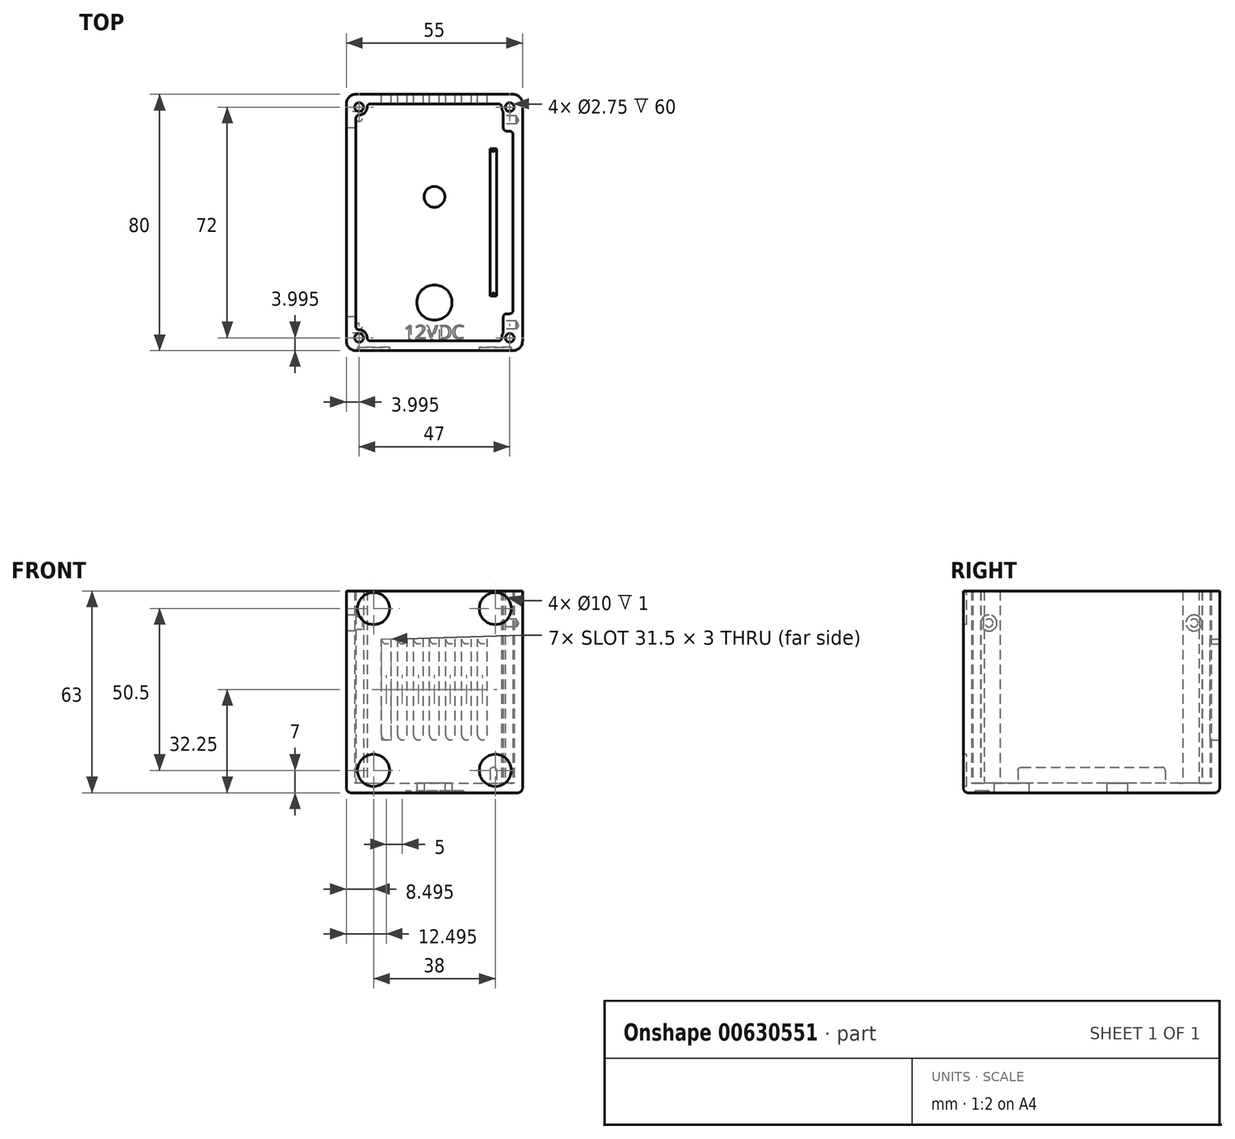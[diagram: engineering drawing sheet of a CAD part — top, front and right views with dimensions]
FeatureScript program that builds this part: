
annotation { "Feature Type Name" : "Feature", "Feature Type Description" : "" }
export const myFeature = defineFeature(function(context is Context, id is Id, definition is map)
    precondition{}
    {
        {
            var Q0;
            Q0=qCreatedBy(makeId("Top.planeOp"),FACE);
            var sketch = newSketch(context, id + "F0", { "sketchPlane" : qUnion([Q0])});
            skLineSegment(sketch, "E0.bottom", {"start": v(-24.01, 49.08) * mm, "end": v(30.99, 49.08) * mm});
            skLineSegment(sketch, "E0.top", {"start": v(-24.01, -30.92) * mm, "end": v(30.99, -30.92) * mm});
            skLineSegment(sketch, "E0.left", {"start": v(-24.01, 49.08) * mm, "end": v(-24.01, -30.92) * mm});
            skLineSegment(sketch, "E0.right", {"start": v(30.99, 49.08) * mm, "end": v(30.99, -30.92) * mm});
            skCircle(sketch, "E1", {"center": v(3.49, -15.92) * mm, "radius": 5.5 * mm});
            skCircle(sketch, "E2", {"center": v(3.49, 17.08) * mm, "radius": 3.25 * mm});
            skSolve(sketch);
        }
        {
            var Q0;
            Q0=makeQuery(id+"F0.imprint","IMPRINT",FACE,{"disambiguationData":[TD([[makeQuery(id+"F0.imprint","IMPRINT",EDGE,{"derivedFrom":sQuery(id+"F0.wireOp",EDGE,"E0.bottom")}),-1.0]])]});
            extrude(context, id + "F1", {"entities" : qUnion([Q0]), "depth" : 3 * mm, "offsetDistance" : 25 * mm});
        }
        {
            var Q0;
            Q0=makeQuery(id+"F1.opExtrude","CAP_FACE",FACE,{"disambiguationData":[OSD([sQuery(id+"F0.wireOp",EDGE,"E0.bottom"),sQuery(id+"F0.wireOp",EDGE,"E0.top"),sQuery(id+"F0.wireOp",EDGE,"E0.left"),sQuery(id+"F0.wireOp",EDGE,"E0.right"),sQuery(id+"F0.wireOp",EDGE,"E1")])],"isStart":false});
            var sketch = newSketch(context, id + "F2", { "sketchPlane" : qUnion([Q0])});
            skLineSegment(sketch, "E3.bottom", {"start": v(-24.01, 49.08) * mm, "end": v(30.99, 49.08) * mm});
            skLineSegment(sketch, "E3.top", {"start": v(-24.01, -30.92) * mm, "end": v(30.99, -30.92) * mm});
            skLineSegment(sketch, "E3.left", {"start": v(-24.01, 49.08) * mm, "end": v(-24.01, -30.92) * mm});
            skLineSegment(sketch, "E3.right", {"start": v(30.99, 49.08) * mm, "end": v(30.99, -30.92) * mm});
            skLineSegment(sketch, "E4.bottom", {"start": v(-16.51, 46.08) * mm, "end": v(23.49, 46.08) * mm});
            skLineSegment(sketch, "E4.top", {"start": v(-16.51, -27.92) * mm, "end": v(23.49, -27.92) * mm});
            skLineSegment(sketch, "E4.left", {"start": v(-21.01, 41.58) * mm, "end": v(-21.01, -23.42) * mm});
            skLineSegment(sketch, "E4.right", {"start": v(27.99, 36.58) * mm, "end": v(27.99, -18.42) * mm});
            skCircle(sketch, "E5", {"center": v(-20.01, 45.08) * mm, "radius": 1.38 * mm});
            skCircle(sketch, "E6", {"center": v(-20.01, 45.08) * mm, "radius": 2.5 * mm});
            skCircle(sketch, "E7", {"center": v(26.99, 45.08) * mm, "radius": 1.38 * mm});
            skCircle(sketch, "E8", {"center": v(26.99, 45.08) * mm, "radius": 2.5 * mm});
            skCircle(sketch, "E9", {"center": v(-20.01, -26.92) * mm, "radius": 1.38 * mm});
            skCircle(sketch, "E10", {"center": v(-20.01, -26.92) * mm, "radius": 2.5 * mm});
            skCircle(sketch, "E11", {"center": v(26.99, -26.92) * mm, "radius": 1.38 * mm});
            skCircle(sketch, "E12", {"center": v(26.99, -26.92) * mm, "radius": 2.5 * mm});
            skLineSegment(sketch, "E13", {"start": v(-20.01, 42.58) * mm, "end": v(-20.01, 42.58) * mm});
            skLineSegment(sketch, "E14", {"start": v(-17.51, 45.08) * mm, "end": v(-17.51, 45.08) * mm});
            skArc(sketch, "E15.filletArc", {"start": v(-16.51, 46.08) * mm, "mid": v(-17.22, 45.78) * mm, "end": v(-17.51, 45.08) * mm});
            skArc(sketch, "E16.filletArc", {"start": v(-20.01, 42.58) * mm, "mid": v(-20.72, 42.28) * mm, "end": v(-21.01, 41.58) * mm});
            skLineSegment(sketch, "E17", {"start": v(24.49, 45.08) * mm, "end": v(24.49, 45.08) * mm});
            skLineSegment(sketch, "E18", {"start": v(26.99, 42.58) * mm, "end": v(26.99, 42.58) * mm});
            skArc(sketch, "E19.filletArc", {"start": v(24.49, 45.08) * mm, "mid": v(24.2, 45.78) * mm, "end": v(23.49, 46.08) * mm});
            skArc(sketch, "E20.filletArc", {"start": v(27.99, 41.58) * mm, "mid": v(27.7, 42.28) * mm, "end": v(26.99, 42.58) * mm});
            skLineSegment(sketch, "E21", {"start": v(-20.01, -24.42) * mm, "end": v(-20.01, -24.42) * mm});
            skLineSegment(sketch, "E22", {"start": v(-17.51, -26.92) * mm, "end": v(-17.51, -26.92) * mm});
            skArc(sketch, "E23.filletArc", {"start": v(-21.01, -23.42) * mm, "mid": v(-20.72, -24.13) * mm, "end": v(-20.01, -24.42) * mm});
            skArc(sketch, "E24.filletArc", {"start": v(-17.51, -26.92) * mm, "mid": v(-17.22, -27.63) * mm, "end": v(-16.51, -27.92) * mm});
            skLineSegment(sketch, "E25", {"start": v(24.49, -26.92) * mm, "end": v(24.49, -26.92) * mm});
            skLineSegment(sketch, "E26", {"start": v(26.99, -24.42) * mm, "end": v(26.99, -24.42) * mm});
            skArc(sketch, "E27.filletArc", {"start": v(23.49, -27.92) * mm, "mid": v(24.2, -27.63) * mm, "end": v(24.49, -26.92) * mm});
            skLineSegment(sketch, "E28.bottom", {"start": v(27.99, 43.58) * mm, "end": v(24.99, 43.58) * mm});
            skLineSegment(sketch, "E28.top", {"start": v(26.99, 37.58) * mm, "end": v(25.99, 37.58) * mm});
            skLineSegment(sketch, "E28.left", {"start": v(27.99, 43.58) * mm, "end": v(27.99, 37.58) * mm});
            skLineSegment(sketch, "E28.right", {"start": v(24.99, 43.58) * mm, "end": v(24.99, 38.58) * mm});
            skLineSegment(sketch, "E29.bottom", {"start": v(26.99, -19.42) * mm, "end": v(25.99, -19.42) * mm});
            skLineSegment(sketch, "E29.top", {"start": v(27.99, -25.42) * mm, "end": v(24.99, -25.42) * mm});
            skLineSegment(sketch, "E29.left", {"start": v(27.99, -19.42) * mm, "end": v(27.99, -25.42) * mm});
            skLineSegment(sketch, "E29.right", {"start": v(24.99, -20.42) * mm, "end": v(24.99, -25.42) * mm});
            skArc(sketch, "E30.filletArc", {"start": v(26.99, -19.42) * mm, "mid": v(27.7, -19.13) * mm, "end": v(27.99, -18.42) * mm});
            skPoint(sketch, "E31.visualSharp", {"position": v(24.99, -19.42) * mm});
            skArc(sketch, "E31.filletArc", {"start": v(25.99, -19.42) * mm, "mid": v(25.28, -19.72) * mm, "end": v(24.99, -20.42) * mm});
            skPoint(sketch, "E32.newPointA", {"position": v(27.99, 37.58) * mm});
            skArc(sketch, "E32.filletArc", {"start": v(27.99, 36.58) * mm, "mid": v(27.7, 37.28) * mm, "end": v(26.99, 37.58) * mm});
            skPoint(sketch, "E33.visualSharp", {"position": v(24.99, 37.58) * mm});
            skArc(sketch, "E33.filletArc", {"start": v(24.99, 38.58) * mm, "mid": v(25.28, 37.87) * mm, "end": v(25.99, 37.58) * mm});
            skLineSegment(sketch, "E34.bottom", {"start": v(20.89, 32.08) * mm, "end": v(22.89, 32.08) * mm});
            skLineSegment(sketch, "E34.top", {"start": v(20.89, -13.84) * mm, "end": v(22.89, -13.84) * mm});
            skLineSegment(sketch, "E34.left", {"start": v(20.89, 32.08) * mm, "end": v(20.89, -13.84) * mm});
            skLineSegment(sketch, "E34.right", {"start": v(22.89, 32.08) * mm, "end": v(22.89, -13.84) * mm});
            skSolve(sketch);
        }
        {
            var Q0;
            Q0=makeQuery(id+"F1.opExtrude","SWEPT_EDGE",EDGE,{"disambiguationData":[OSD([sQuery(id+"F0.wireOp",EDGE,"E0.top"),sQuery(id+"F0.wireOp",EDGE,"E0.right")])]});
            var Q1;
            Q1=makeQuery(id+"F1.opExtrude","SWEPT_EDGE",EDGE,{"disambiguationData":[OSD([sQuery(id+"F0.wireOp",EDGE,"E0.top"),sQuery(id+"F0.wireOp",EDGE,"E0.left")])]});
            var Q2;
            Q2=makeQuery(id+"F1.opExtrude","SWEPT_EDGE",EDGE,{"disambiguationData":[OSD([sQuery(id+"F0.wireOp",EDGE,"E0.bottom"),sQuery(id+"F0.wireOp",EDGE,"E0.left")])]});
            var Q3;
            Q3=makeQuery(id+"F1.opExtrude","SWEPT_EDGE",EDGE,{"disambiguationData":[OSD([sQuery(id+"F0.wireOp",EDGE,"E0.bottom"),sQuery(id+"F0.wireOp",EDGE,"E0.right")])]});
            fillet(context, id + "F3", {"entities" : qUnion([Q0, Q1, Q2, Q3]), "radius" : 3 * mm, "tangentPropagation" : true, "allowEdgeOverflow" : false});
        }
        {
            var Q0;
            Q0=makeQuery(id+"F1.opExtrude","CAP_EDGE",EDGE,{"disambiguationData":[OSD([sQuery(id+"F0.wireOp",EDGE,"E0.right")])],"isStart":true});
            fillet(context, id + "F4", {"entities" : qUnion([Q0]), "radius" : 1.5 * mm, "tangentPropagation" : true, "allowEdgeOverflow" : false});
        }
        {
            var Q0;
            Q0=makeQuery(id+"F2.imprint","IMPRINT",FACE,{"disambiguationData":[TD([[makeQuery(id+"F2.imprint","IMPRINT",EDGE,{"derivedFrom":sQuery(id+"F2.wireOp",EDGE,"E9")}),-1.0]])]});
            var Q1;
            Q1=makeQuery(id+"F2.imprint","IMPRINT",FACE,{"disambiguationData":[TD([[makeQuery(id+"F2.imprint","IMPRINT",EDGE,{"derivedFrom":sQuery(id+"F2.wireOp",EDGE,"E11")}),-1.0]])]});
            var Q2;
            {var subQ0=sQuery(id+"F2.wireOp",EDGE,"E29.top");Q2=makeQuery(id+"F2.imprint","IMPRINT",FACE,{"disambiguationData":[TD([[makeQuery(id+"F2.imprint","IMPRINT",EDGE,{"derivedFrom":subQ0}),-1.0]])]});}
            var Q3;
            Q3=makeQuery(id+"F2.imprint","IMPRINT",FACE,{"disambiguationData":[TD([[makeQuery(id+"F2.imprint","IMPRINT",EDGE,{"derivedFrom":sQuery(id+"F2.wireOp",EDGE,"E5")}),-1.0]])]});
            var Q4;
            Q4=makeQuery(id+"F2.imprint","IMPRINT",FACE,{"disambiguationData":[TD([[makeQuery(id+"F2.imprint","IMPRINT",EDGE,{"derivedFrom":sQuery(id+"F2.wireOp",EDGE,"E7")}),-1.0]])]});
            var Q5;
            {var subQ2=sQuery(id+"F2.wireOp",EDGE,"E28.bottom");Q5=makeQuery(id+"F2.imprint","IMPRINT",FACE,{"disambiguationData":[TD([[makeQuery(id+"F2.imprint","IMPRINT",EDGE,{"derivedFrom":subQ2}),1.0]])]});}
            var Q6;
            Q6=makeQuery(id+"F2.imprint","IMPRINT",FACE,{"disambiguationData":[TD([[makeQuery(id+"F2.imprint","IMPRINT",EDGE,{"derivedFrom":sQuery(id+"F2.wireOp",EDGE,"E3.bottom")}),-1.0]])]});
            var Q7;
            {var subQ0=sQuery(id+"F2.wireOp",EDGE,"E20.filletArc");Q7=makeQuery(id+"F2.imprint","IMPRINT",FACE,{"disambiguationData":[TD([[makeQuery(id+"F2.imprint","IMPRINT",EDGE,{"derivedFrom":subQ0}),-1.0]])]});}
            extrude(context, id + "F5", {"entities" : qUnion([Q0, Q1, Q2, Q3, Q4, Q5, Q6, Q7]), "operationType" : NewBodyOperationType.ADD, "depth" : 60 * mm, "offsetDistance" : 25 * mm});
        }
        {
            var Q0;
            Q0=makeQuery(id+"F5.opExtrude","SWEPT_EDGE",EDGE,{"disambiguationData":[OSD([sQuery(id+"F2.wireOp",EDGE,"E3.bottom"),sQuery(id+"F2.wireOp",EDGE,"E3.left")])]});
            var Q1;
            Q1=makeQuery(id+"F5.opExtrude","SWEPT_EDGE",EDGE,{"disambiguationData":[OSD([sQuery(id+"F2.wireOp",EDGE,"E3.top"),sQuery(id+"F2.wireOp",EDGE,"E3.left")])]});
            var Q2;
            Q2=makeQuery(id+"F5.opExtrude","SWEPT_EDGE",EDGE,{"disambiguationData":[OSD([sQuery(id+"F2.wireOp",EDGE,"E3.bottom"),sQuery(id+"F2.wireOp",EDGE,"E3.right")])]});
            var Q3;
            Q3=makeQuery(id+"F5.opExtrude","SWEPT_EDGE",EDGE,{"disambiguationData":[OSD([sQuery(id+"F2.wireOp",EDGE,"E3.top"),sQuery(id+"F2.wireOp",EDGE,"E3.right")])]});
            fillet(context, id + "F6", {"entities" : qUnion([Q0, Q1, Q2, Q3]), "radius" : 3 * mm, "tangentPropagation" : true, "allowEdgeOverflow" : false});
        }
        {
            var Q0;
            Q0=makeQuery(id+"F5.opExtrude","SWEPT_FACE",FACE,{"disambiguationData":[OSD([sQuery(id+"F2.wireOp",EDGE,"E29.right")])]});
            var sketch = newSketch(context, id + "F7", { "sketchPlane" : qUnion([Q0])});
            skPoint(sketch, "E35", {"position": v(-41.08, 53) * mm});
            skPoint(sketch, "E36", {"position": v(-41.08, 8.5) * mm});
            skPoint(sketch, "E37", {"position": v(22.92, 8.5) * mm});
            skPoint(sketch, "E38", {"position": v(22.92, 53) * mm});
            skSolve(sketch);
        }
        {
            var Q0;
            Q0=sQuery(id+"F7.wireOp",VERTEX,"E35");
            var Q1;
            Q1=sQuery(id+"F7.wireOp",VERTEX,"E38");
            var Q2;
            Q2=makeQuery(id+"F1.opExtrude","SWEPT_BODY",BODY,{"disambiguationData":[OSD([sQuery(id+"F0.wireOp",EDGE,"E0.bottom"),sQuery(id+"F0.wireOp",EDGE,"E0.top"),sQuery(id+"F0.wireOp",EDGE,"E0.left"),sQuery(id+"F0.wireOp",EDGE,"E0.right"),sQuery(id+"F0.wireOp",EDGE,"E1")])]});
            hole(context, id + "F8", {"style" : HoleStyle.SIMPLE, "endStyle" : HoleEndStyle.BLIND, "holeDiameter" : 2.5 * mm, "majorDiameter" : 5 * mm, "holeDepth" : 4 * mm, "isTappedThrough" : true, "tappedDepth" : 12 * mm, "tapClearance" : 3, "locations" : qUnion([Q0, Q1]), "scope" : qUnion([Q2])});
        }
        {
            var Q0;
            Q0=makeQuery(id+"F5.boolean.opBoolean","MERGE",FACE,{"derivedFrom":[makeQuery(id+"F1.opExtrude","SWEPT_FACE",FACE,{"disambiguationData":[OSD([sQuery(id+"F0.wireOp",EDGE,"E0.bottom")])]}),makeQuery(id+"F5.opExtrude","SWEPT_FACE",FACE,{"disambiguationData":[OSD([sQuery(id+"F2.wireOp",EDGE,"E3.bottom")])]})]});
            var sketch = newSketch(context, id + "F9", { "sketchPlane" : qUnion([Q0])});
            skCircle(sketch, "E39", {"center": v(-18.49, 18) * mm, "radius": 1.5 * mm});
            skCircle(sketch, "E40.0.1.0", {"center": v(-18.49, 48) * mm, "radius": 1.5 * mm});
            skLineSegment(sketch, "E40.direction2", {"start": v(-18.49, 18) * mm, "end": v(-18.49, 48) * mm, "construction": true});
            skLineSegment(sketch, "E41", {"start": v(-16.99, 18) * mm, "end": v(-16.99, 48) * mm});
            skLineSegment(sketch, "E42", {"start": v(-19.99, 18) * mm, "end": v(-19.99, 48) * mm});
            skCircle(sketch, "E43.1.0.0", {"center": v(-13.49, 18) * mm, "radius": 1.5 * mm});
            skLineSegment(sketch, "E43.1.0.1", {"start": v(-11.99, 18) * mm, "end": v(-11.99, 48) * mm});
            skCircle(sketch, "E43.1.0.2", {"center": v(-13.49, 48) * mm, "radius": 1.5 * mm});
            skLineSegment(sketch, "E43.1.0.3", {"start": v(-14.99, 18) * mm, "end": v(-14.99, 48) * mm});
            skCircle(sketch, "E43.2.0.0", {"center": v(-8.49, 18) * mm, "radius": 1.5 * mm});
            skLineSegment(sketch, "E43.2.0.1", {"start": v(-6.99, 18) * mm, "end": v(-6.99, 48) * mm});
            skCircle(sketch, "E43.2.0.2", {"center": v(-8.49, 48) * mm, "radius": 1.5 * mm});
            skLineSegment(sketch, "E43.2.0.3", {"start": v(-9.99, 18) * mm, "end": v(-9.99, 48) * mm});
            skCircle(sketch, "E43.3.0.0", {"center": v(-3.49, 18) * mm, "radius": 1.5 * mm});
            skLineSegment(sketch, "E43.3.0.1", {"start": v(-1.99, 18) * mm, "end": v(-1.99, 48) * mm});
            skCircle(sketch, "E43.3.0.2", {"center": v(-3.49, 48) * mm, "radius": 1.5 * mm});
            skLineSegment(sketch, "E43.3.0.3", {"start": v(-4.99, 18) * mm, "end": v(-4.99, 48) * mm});
            skCircle(sketch, "E43.4.0.0", {"center": v(1.51, 18) * mm, "radius": 1.5 * mm});
            skLineSegment(sketch, "E43.4.0.1", {"start": v(3.01, 18) * mm, "end": v(3.01, 48) * mm});
            skCircle(sketch, "E43.4.0.2", {"center": v(1.51, 48) * mm, "radius": 1.5 * mm});
            skLineSegment(sketch, "E43.4.0.3", {"start": v(0.01, 18) * mm, "end": v(0.01, 48) * mm});
            skCircle(sketch, "E43.5.0.0", {"center": v(6.51, 18) * mm, "radius": 1.5 * mm});
            skLineSegment(sketch, "E43.5.0.1", {"start": v(8.01, 18) * mm, "end": v(8.01, 48) * mm});
            skCircle(sketch, "E43.5.0.2", {"center": v(6.51, 48) * mm, "radius": 1.5 * mm});
            skLineSegment(sketch, "E43.5.0.3", {"start": v(5.01, 18) * mm, "end": v(5.01, 48) * mm});
            skCircle(sketch, "E43.6.0.0", {"center": v(11.51, 18) * mm, "radius": 1.5 * mm});
            skLineSegment(sketch, "E43.6.0.1", {"start": v(13.01, 18) * mm, "end": v(13.01, 48) * mm});
            skCircle(sketch, "E43.6.0.2", {"center": v(11.51, 48) * mm, "radius": 1.5 * mm});
            skLineSegment(sketch, "E43.6.0.3", {"start": v(10.01, 18) * mm, "end": v(10.01, 48) * mm});
            skLineSegment(sketch, "E43.direction1", {"start": v(-18.49, 18) * mm, "end": v(-13.49, 18) * mm, "construction": true});
            skSolve(sketch);
        }
        {
            var Q0;
            {var subQ0=sQuery(id+"F9.wireOp",EDGE,"E43.6.0.1");Q0=makeQuery(id+"F9.imprint","IMPRINT",FACE,{"disambiguationData":[TD([[makeQuery(id+"F9.imprint","IMPRINT",EDGE,{"derivedFrom":subQ0}),1.0]])]});}
            var Q1;
            {var subQ0=sQuery(id+"F9.wireOp",EDGE,"E43.5.0.1");Q1=makeQuery(id+"F9.imprint","IMPRINT",FACE,{"disambiguationData":[TD([[makeQuery(id+"F9.imprint","IMPRINT",EDGE,{"derivedFrom":subQ0}),1.0]])]});}
            var Q2;
            {var subQ0=sQuery(id+"F9.wireOp",EDGE,"E43.4.0.1");Q2=makeQuery(id+"F9.imprint","IMPRINT",FACE,{"disambiguationData":[TD([[makeQuery(id+"F9.imprint","IMPRINT",EDGE,{"derivedFrom":subQ0}),1.0]])]});}
            var Q3;
            {var subQ0=sQuery(id+"F9.wireOp",EDGE,"E43.3.0.1");Q3=makeQuery(id+"F9.imprint","IMPRINT",FACE,{"disambiguationData":[TD([[makeQuery(id+"F9.imprint","IMPRINT",EDGE,{"derivedFrom":subQ0}),1.0]])]});}
            var Q4;
            {var subQ0=sQuery(id+"F9.wireOp",EDGE,"E43.2.0.1");Q4=makeQuery(id+"F9.imprint","IMPRINT",FACE,{"disambiguationData":[TD([[makeQuery(id+"F9.imprint","IMPRINT",EDGE,{"derivedFrom":subQ0}),1.0]])]});}
            var Q5;
            {var subQ0=sQuery(id+"F9.wireOp",EDGE,"E43.1.0.1");Q5=makeQuery(id+"F9.imprint","IMPRINT",FACE,{"disambiguationData":[TD([[makeQuery(id+"F9.imprint","IMPRINT",EDGE,{"derivedFrom":subQ0}),1.0]])]});}
            var Q6;
            {var subQ0=sQuery(id+"F9.wireOp",EDGE,"E41");Q6=makeQuery(id+"F9.imprint","IMPRINT",FACE,{"disambiguationData":[TD([[makeQuery(id+"F9.imprint","IMPRINT",EDGE,{"derivedFrom":subQ0}),1.0]])]});}
            var Q7;
            {var subQ0=sQuery(id+"F9.wireOp",EDGE,"E39");var subQ1=makeQuery(id+"F9.imprint","INTERSECT",VERTEX,{"derivedFrom":[subQ0,sQuery(id+"F9.wireOp",EDGE,"E41")]});Q7=makeQuery(id+"F9.imprint","IMPRINT",FACE,{"disambiguationData":[TD([[makeQuery(id+"F9.imprint","IMPRINT",EDGE,{"disambiguationData":[TD([[subQ1,-1.0]])],"derivedFrom":subQ0}),1.0]])]});}
            var Q8;
            {var subQ0=sQuery(id+"F9.wireOp",EDGE,"E43.1.0.0");var subQ1=makeQuery(id+"F9.imprint","INTERSECT",VERTEX,{"derivedFrom":[subQ0,sQuery(id+"F9.wireOp",EDGE,"E43.1.0.1")]});Q8=makeQuery(id+"F9.imprint","IMPRINT",FACE,{"disambiguationData":[TD([[makeQuery(id+"F9.imprint","IMPRINT",EDGE,{"disambiguationData":[TD([[subQ1,-1.0]])],"derivedFrom":subQ0}),1.0]])]});}
            var Q9;
            {var subQ0=sQuery(id+"F9.wireOp",EDGE,"E43.2.0.0");var subQ1=makeQuery(id+"F9.imprint","INTERSECT",VERTEX,{"derivedFrom":[subQ0,sQuery(id+"F9.wireOp",EDGE,"E43.2.0.1")]});Q9=makeQuery(id+"F9.imprint","IMPRINT",FACE,{"disambiguationData":[TD([[makeQuery(id+"F9.imprint","IMPRINT",EDGE,{"disambiguationData":[TD([[subQ1,-1.0]])],"derivedFrom":subQ0}),1.0]])]});}
            var Q10;
            {var subQ0=sQuery(id+"F9.wireOp",EDGE,"E43.3.0.0");var subQ1=makeQuery(id+"F9.imprint","INTERSECT",VERTEX,{"derivedFrom":[subQ0,sQuery(id+"F9.wireOp",EDGE,"E43.3.0.1")]});Q10=makeQuery(id+"F9.imprint","IMPRINT",FACE,{"disambiguationData":[TD([[makeQuery(id+"F9.imprint","IMPRINT",EDGE,{"disambiguationData":[TD([[subQ1,-1.0]])],"derivedFrom":subQ0}),1.0]])]});}
            var Q11;
            {var subQ0=sQuery(id+"F9.wireOp",EDGE,"E43.4.0.0");var subQ1=makeQuery(id+"F9.imprint","INTERSECT",VERTEX,{"derivedFrom":[subQ0,sQuery(id+"F9.wireOp",EDGE,"E43.4.0.1")]});Q11=makeQuery(id+"F9.imprint","IMPRINT",FACE,{"disambiguationData":[TD([[makeQuery(id+"F9.imprint","IMPRINT",EDGE,{"disambiguationData":[TD([[subQ1,-1.0]])],"derivedFrom":subQ0}),1.0]])]});}
            var Q12;
            {var subQ0=sQuery(id+"F9.wireOp",EDGE,"E43.5.0.0");var subQ1=makeQuery(id+"F9.imprint","INTERSECT",VERTEX,{"derivedFrom":[subQ0,sQuery(id+"F9.wireOp",EDGE,"E43.5.0.1")]});Q12=makeQuery(id+"F9.imprint","IMPRINT",FACE,{"disambiguationData":[TD([[makeQuery(id+"F9.imprint","IMPRINT",EDGE,{"disambiguationData":[TD([[subQ1,-1.0]])],"derivedFrom":subQ0}),1.0]])]});}
            var Q13;
            {var subQ0=sQuery(id+"F9.wireOp",EDGE,"E43.6.0.0");var subQ1=makeQuery(id+"F9.imprint","INTERSECT",VERTEX,{"derivedFrom":[subQ0,sQuery(id+"F9.wireOp",EDGE,"E43.6.0.1")]});Q13=makeQuery(id+"F9.imprint","IMPRINT",FACE,{"disambiguationData":[TD([[makeQuery(id+"F9.imprint","IMPRINT",EDGE,{"disambiguationData":[TD([[subQ1,-1.0]])],"derivedFrom":subQ0}),1.0]])]});}
            var Q14;
            {var subQ0=sQuery(id+"F9.wireOp",EDGE,"E43.6.0.2");var subQ2=makeQuery(id+"F9.imprint","IMPRINT",VERTEX,{"derivedFrom":subQ0});Q14=makeQuery(id+"F9.imprint","IMPRINT",FACE,{"disambiguationData":[TD([[makeQuery(id+"F9.imprint","IMPRINT",EDGE,{"disambiguationData":[TD([[subQ2,1.0]])],"derivedFrom":subQ0}),1.0]])]});}
            var Q15;
            {var subQ0=sQuery(id+"F9.wireOp",EDGE,"E43.5.0.2");var subQ2=makeQuery(id+"F9.imprint","IMPRINT",VERTEX,{"derivedFrom":subQ0});Q15=makeQuery(id+"F9.imprint","IMPRINT",FACE,{"disambiguationData":[TD([[makeQuery(id+"F9.imprint","IMPRINT",EDGE,{"disambiguationData":[TD([[subQ2,1.0]])],"derivedFrom":subQ0}),1.0]])]});}
            var Q16;
            {var subQ0=sQuery(id+"F9.wireOp",EDGE,"E43.4.0.2");var subQ2=makeQuery(id+"F9.imprint","IMPRINT",VERTEX,{"derivedFrom":subQ0});Q16=makeQuery(id+"F9.imprint","IMPRINT",FACE,{"disambiguationData":[TD([[makeQuery(id+"F9.imprint","IMPRINT",EDGE,{"disambiguationData":[TD([[subQ2,1.0]])],"derivedFrom":subQ0}),1.0]])]});}
            var Q17;
            {var subQ0=sQuery(id+"F9.wireOp",EDGE,"E43.3.0.2");var subQ2=makeQuery(id+"F9.imprint","IMPRINT",VERTEX,{"derivedFrom":subQ0});Q17=makeQuery(id+"F9.imprint","IMPRINT",FACE,{"disambiguationData":[TD([[makeQuery(id+"F9.imprint","IMPRINT",EDGE,{"disambiguationData":[TD([[subQ2,1.0]])],"derivedFrom":subQ0}),1.0]])]});}
            var Q18;
            {var subQ0=sQuery(id+"F9.wireOp",EDGE,"E43.2.0.2");var subQ2=makeQuery(id+"F9.imprint","IMPRINT",VERTEX,{"derivedFrom":subQ0});Q18=makeQuery(id+"F9.imprint","IMPRINT",FACE,{"disambiguationData":[TD([[makeQuery(id+"F9.imprint","IMPRINT",EDGE,{"disambiguationData":[TD([[subQ2,1.0]])],"derivedFrom":subQ0}),1.0]])]});}
            var Q19;
            {var subQ0=sQuery(id+"F9.wireOp",EDGE,"E43.1.0.2");var subQ2=makeQuery(id+"F9.imprint","IMPRINT",VERTEX,{"derivedFrom":subQ0});Q19=makeQuery(id+"F9.imprint","IMPRINT",FACE,{"disambiguationData":[TD([[makeQuery(id+"F9.imprint","IMPRINT",EDGE,{"disambiguationData":[TD([[subQ2,1.0]])],"derivedFrom":subQ0}),1.0]])]});}
            var Q20;
            {var subQ0=sQuery(id+"F9.wireOp",EDGE,"E40.0.1.0");var subQ2=makeQuery(id+"F9.imprint","IMPRINT",VERTEX,{"derivedFrom":subQ0});Q20=makeQuery(id+"F9.imprint","IMPRINT",FACE,{"disambiguationData":[TD([[makeQuery(id+"F9.imprint","IMPRINT",EDGE,{"disambiguationData":[TD([[subQ2,1.0]])],"derivedFrom":subQ0}),1.0]])]});}
            extrude(context, id + "F10", {"entities" : qUnion([Q0, Q1, Q2, Q3, Q4, Q5, Q6, Q7, Q8, Q9, Q10, Q11, Q12, Q13, Q14, Q15, Q16, Q17, Q18, Q19, Q20]), "operationType" : NewBodyOperationType.REMOVE, "oppositeDirection" : true, "depth" : 5 * mm, "offsetDistance" : 25 * mm});
        }
        {
            var Q0;
            Q0=makeQuery(id+"F5.boolean.opBoolean","MERGE",FACE,{"derivedFrom":[makeQuery(id+"F1.opExtrude","SWEPT_FACE",FACE,{"disambiguationData":[OSD([sQuery(id+"F0.wireOp",EDGE,"E0.top")])]}),makeQuery(id+"F5.opExtrude","SWEPT_FACE",FACE,{"disambiguationData":[OSD([sQuery(id+"F2.wireOp",EDGE,"E3.top")])]})]});
            var sketch = newSketch(context, id + "F11", { "sketchPlane" : qUnion([Q0])});
            skPoint(sketch, "E44", {"position": v(-15.51, 57.5) * mm});
            skPoint(sketch, "E45", {"position": v(22.49, 57.5) * mm});
            skPoint(sketch, "E46", {"position": v(22.49, 7) * mm});
            skPoint(sketch, "E47", {"position": v(-15.51, 7) * mm});
            skCircle(sketch, "E48", {"center": v(-15.51, 57.5) * mm, "radius": 5 * mm});
            skCircle(sketch, "E49", {"center": v(22.49, 57.5) * mm, "radius": 5 * mm});
            skCircle(sketch, "E50", {"center": v(-15.51, 7) * mm, "radius": 5 * mm});
            skCircle(sketch, "E51", {"center": v(22.49, 7) * mm, "radius": 5 * mm});
            skSolve(sketch);
        }
        {
            var Q0;
            Q0=makeQuery(id+"F11.imprint","IMPRINT",FACE,{"disambiguationData":[TD([[makeQuery(id+"F11.imprint","IMPRINT",EDGE,{"derivedFrom":sQuery(id+"F11.wireOp",EDGE,"E48")}),1.0]])]});
            var Q1;
            Q1=makeQuery(id+"F11.imprint","IMPRINT",FACE,{"disambiguationData":[TD([[makeQuery(id+"F11.imprint","IMPRINT",EDGE,{"derivedFrom":sQuery(id+"F11.wireOp",EDGE,"E49")}),1.0]])]});
            var Q2;
            Q2=makeQuery(id+"F11.imprint","IMPRINT",FACE,{"disambiguationData":[TD([[makeQuery(id+"F11.imprint","IMPRINT",EDGE,{"derivedFrom":sQuery(id+"F11.wireOp",EDGE,"E51")}),1.0]])]});
            var Q3;
            Q3=makeQuery(id+"F11.imprint","IMPRINT",FACE,{"disambiguationData":[TD([[makeQuery(id+"F11.imprint","IMPRINT",EDGE,{"derivedFrom":sQuery(id+"F11.wireOp",EDGE,"E50")}),1.0]])]});
            var Q4;
            Q4=makeQuery(id+"F11.imprint","IMPRINT",FACE,{"disambiguationData":[TD([[makeQuery(id+"F11.imprint","IMPRINT",EDGE,{"derivedFrom":sQuery(id+"F11.wireOp",EDGE,"E50")}),1.0]])]});
            extrude(context, id + "F12", {"entities" : qUnion([Q0, Q1, Q2, Q3, Q4]), "operationType" : NewBodyOperationType.REMOVE, "oppositeDirection" : true, "depth" : 1 * mm, "offsetDistance" : 25 * mm});
        }
        {
            var Q0;
            Q0=makeQuery(id+"F5.boolean.opBoolean","MERGE",FACE,{"derivedFrom":[makeQuery(id+"F1.opExtrude","SWEPT_FACE",FACE,{"disambiguationData":[OSD([sQuery(id+"F0.wireOp",EDGE,"E0.left")])]}),makeQuery(id+"F5.opExtrude","SWEPT_FACE",FACE,{"disambiguationData":[OSD([sQuery(id+"F2.wireOp",EDGE,"E3.left")])]})]});
            var sketch = newSketch(context, id + "F13", { "sketchPlane" : qUnion([Q0])});
            skCircle(sketch, "E52", {"center": v(-41.08, 53) * mm, "radius": 2.5 * mm});
            skCircle(sketch, "E53", {"center": v(22.92, 53) * mm, "radius": 2.5 * mm});
            skCircle(sketch, "E54", {"center": v(-41.08, 8.5) * mm, "radius": 2.5 * mm});
            skCircle(sketch, "E55", {"center": v(22.92, 8.5) * mm, "radius": 2.5 * mm});
            skSolve(sketch);
        }
        {
            var Q0;
            Q0=makeQuery(id+"F13.imprint","IMPRINT",FACE,{"disambiguationData":[TD([[makeQuery(id+"F13.imprint","IMPRINT",EDGE,{"derivedFrom":sQuery(id+"F13.wireOp",EDGE,"E52")}),1.0]])]});
            var Q1;
            Q1=makeQuery(id+"F13.imprint","IMPRINT",FACE,{"disambiguationData":[TD([[makeQuery(id+"F13.imprint","IMPRINT",EDGE,{"derivedFrom":sQuery(id+"F13.wireOp",EDGE,"E53")}),1.0]])]});
            extrude(context, id + "F14", {"entities" : qUnion([Q0, Q1]), "operationType" : NewBodyOperationType.REMOVE, "oppositeDirection" : true, "depth" : 5 * mm, "offsetDistance" : 25 * mm});
        }
        {
            var Q0;
            Q0=makeQuery(id+"F0.imprint","IMPRINT",FACE,{"disambiguationData":[TD([[makeQuery(id+"F0.imprint","IMPRINT",EDGE,{"derivedFrom":sQuery(id+"F0.wireOp",EDGE,"E0.bottom")}),-1.0]])]});
            var sketch = newSketch(context, id + "F15", { "sketchPlane" : qUnion([Q0])});
            skText(sketch, "E56", { "text": "12VDC", "fontName": "OpenSans-Regular.ttf"});
            const initialGuessF15  = {"E56": [-0.00598, -0.0273, 1, 0, 0.00435]};
            skSetInitialGuess(sketch, initialGuessF15);
            skSolve(sketch);
        }
        {
            var Q0;
            Q0=makeQuery(id+"F2.imprint","IMPRINT",FACE,{"disambiguationData":[TD([[makeQuery(id+"F2.imprint","IMPRINT",EDGE,{"derivedFrom":sQuery(id+"F2.wireOp",EDGE,"E34.bottom")}),-1.0]])]});
            extrude(context, id + "F16", {"entities" : qUnion([Q0]), "operationType" : NewBodyOperationType.ADD, "depth" : 5 * mm, "offsetDistance" : 25 * mm});
        }
        {
            var Q0;
            Q0=makeQuery(id+"F16.opExtrude","CAP_EDGE",EDGE,{"disambiguationData":[OSD([sQuery(id+"F2.wireOp",EDGE,"E34.left")])],"isStart":false});
            var Q1;
            Q1=makeQuery(id+"F16.opExtrude","CAP_EDGE",EDGE,{"disambiguationData":[OSD([sQuery(id+"F2.wireOp",EDGE,"E34.right")])],"isStart":false});
            var Q2;
            Q2=makeQuery(id+"F16.opExtrude","CAP_EDGE",EDGE,{"disambiguationData":[OSD([sQuery(id+"F2.wireOp",EDGE,"E34.bottom")])],"isStart":false});
            var Q3;
            Q3=makeQuery(id+"F16.opExtrude","CAP_EDGE",EDGE,{"disambiguationData":[OSD([sQuery(id+"F2.wireOp",EDGE,"E34.top")])],"isStart":false});
            fillet(context, id + "F17", {"entities" : qUnion([Q0, Q1, Q2, Q3]), "tangentPropagation" : true, "radius" : 1 * mm, "defaultsChanged" : false, "vertexSettings" : [], "allowEdgeOverflow" : false});
        }
        {
            var Q0;
            Q0 = qSketchRegion(id + "F15", true);
            extrude(context, id + "F18", {"entities" : qUnion([Q0]), "operationType" : NewBodyOperationType.REMOVE, "oppositeDirection" : true, "depth" : -.6 * mm, "offsetDistance" : 25 * mm});
        }
    });
